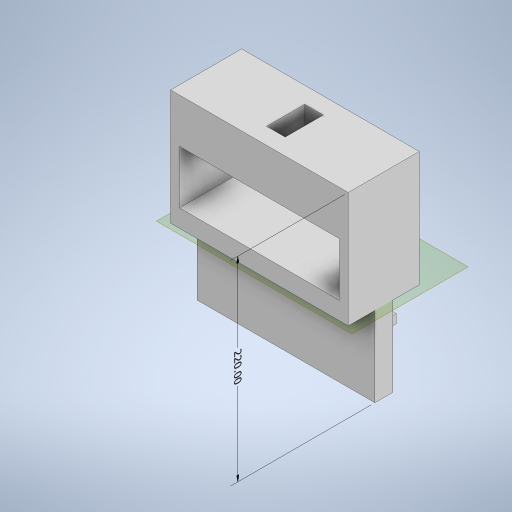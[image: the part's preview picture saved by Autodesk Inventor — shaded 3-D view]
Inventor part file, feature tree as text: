
AUTODESK INVENTOR PART (.ipt)
format: ipt  version: 2023 (Build 270158000, 158)  size: 313,344 bytes
history: native  units: mm
features: extrude x6, sketch x6, other x4, plane x3
ambient origin geometry x8: Origin, YZ Plane, XZ Plane, XY Plane, X Axis, Y Axis, Z Axis, Center Point
bodies: Body1 (feature_tree), Body2 (feature_tree)
feature tree (19):
  other  "Sólido1"
  other  "Anotaciones"
  extrude  "Extrusión1"  Depth=80.0mm
  extrude  "Extrusión2"  Depth=180.0mm
  extrude  "Extrusión3"  Depth=20.0mm
  extrude  "Extrusión4"  Depth=21.0mm
  plane  "Plano de trabajo1"
  extrude  "Extrusión6"  Depth=20.0mm
  plane  "Plano de trabajo3"
  extrude  "Extrusión7"  [1 undecoded]
  plane  "Plano de trabajo4"
  sketch  "Boceto1"  dims[d0=200.0mm d1=80.0mm]
  sketch  "Boceto2"  dims[d2=130.0mm d3=0.0mm d4=180.0mm]
  sketch  "Boceto3"  dims[d5=60.0mm d6=20.0mm]
  sketch  "Boceto4"  dims[d7=60.0mm d8=0.0mm d9=21.0mm d10=43.0mm]
  sketch  "Boceto7"  dims[d11=43.0mm d12=0.0mm d13=20.0mm]
  other  "Sólido3"
  sketch  "Boceto10"  dims[d14=90.0mm d15=0.0mm d16=-90.0mm d28=20.0mm d29=20.0mm d30=30.0mm d31=30.0mm d32=20.0mm d33=35.0mm d34=35.0mm d35=69.0mm d36=10.0mm d37=0.0mm d45=1.5mm d50=10.0mm d51=0.0mm d52=10.0mm d53=89.5mm d54=90.0deg d38=3.166395mm d39=4.283575mm d40=220.0mm]
  other  "Cota lineal 1"
note: 1 required parameter value undecoded (feature->parameter linkage not recoverable at this tier; creation-order binding heuristic only, values carry confidence <= 0.55)
